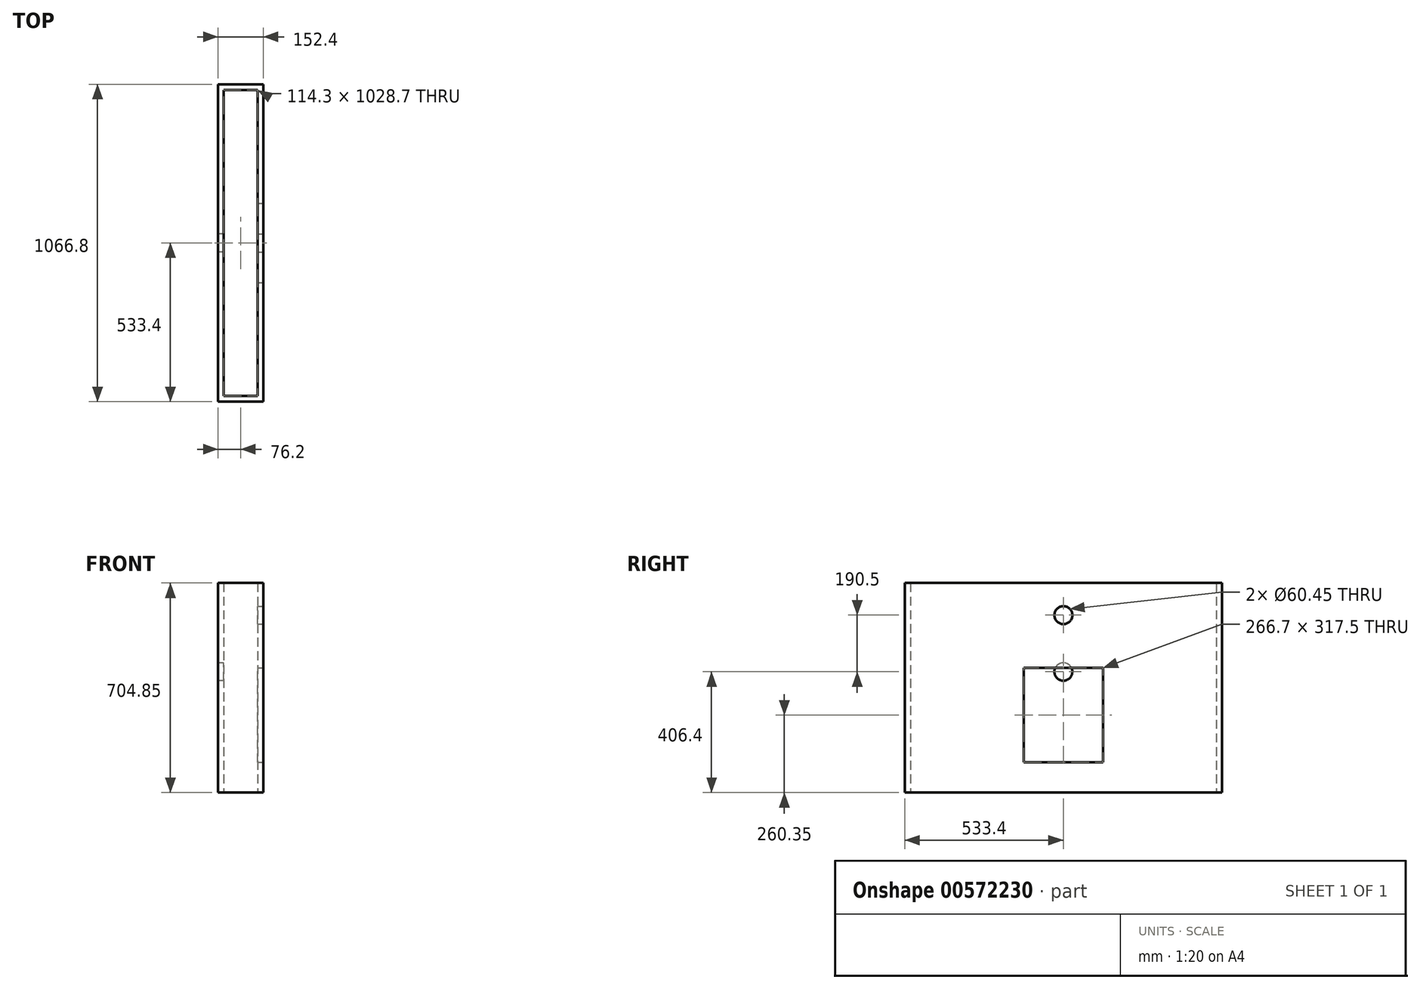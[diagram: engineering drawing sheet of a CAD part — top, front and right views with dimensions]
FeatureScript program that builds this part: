
annotation { "Feature Type Name" : "Feature", "Feature Type Description" : "" }
export const myFeature = defineFeature(function(context is Context, id is Id, definition is map)
    precondition{}
    {
        {
            var Q0;
            Q0=qCreatedBy(makeId("Top.planeOp"),FACE);
            var sketch = newSketch(context, id + "F0", { "sketchPlane" : qUnion([Q0])});
            skLineSegment(sketch, "E0.bottom", {"start": v(76.2, 533.4) * mm, "end": v(-76.2, 533.4) * mm});
            skLineSegment(sketch, "E0.top", {"start": v(76.2, -533.4) * mm, "end": v(-76.2, -533.4) * mm});
            skLineSegment(sketch, "E0.left", {"start": v(76.2, 533.4) * mm, "end": v(76.2, -533.4) * mm});
            skLineSegment(sketch, "E0.right", {"start": v(-76.2, 533.4) * mm, "end": v(-76.2, -533.4) * mm});
            skPoint(sketch, "E0.middle", {"position": v(0, 0) * mm});
            skLineSegment(sketch, "E1.bottom", {"start": v(57.15, 514.35) * mm, "end": v(-57.15, 514.35) * mm});
            skLineSegment(sketch, "E1.top", {"start": v(57.15, -514.35) * mm, "end": v(-57.15, -514.35) * mm});
            skLineSegment(sketch, "E1.left", {"start": v(57.15, 514.35) * mm, "end": v(57.15, -514.35) * mm});
            skLineSegment(sketch, "E1.right", {"start": v(-57.15, 514.35) * mm, "end": v(-57.15, -514.35) * mm});
            skSolve(sketch);
        }
        {
            var Q0;
            Q0=makeQuery(id+"F0.imprint","IMPRINT",FACE,{"disambiguationData":[TD([[makeQuery(id+"F0.imprint","IMPRINT",EDGE,{"derivedFrom":sQuery(id+"F0.wireOp",EDGE,"E0.bottom")}),1.0]])]});
            extrude(context, id + "F1", {"entities" : qUnion([Q0]), "depth" : 704.85 * mm, "offsetDistance" : 25.4 * mm});
        }
        {
            var Q0;
            Q0=makeQuery(id+"F1.opExtrude","SWEPT_FACE",FACE,{"disambiguationData":[OSD([sQuery(id+"F0.wireOp",EDGE,"E0.left")])]});
            var sketch = newSketch(context, id + "F2", { "sketchPlane" : qUnion([Q0])});
            skLineSegment(sketch, "E2", {"start": v(0, 0) * mm, "end": v(0, 101.6) * mm});
            skPoint(sketch, "E2.endSnap0", {"position": v(0, 0) * mm});
            skLineSegment(sketch, "E3", {"start": v(0, 101.6) * mm, "end": v(0, 260.35) * mm});
            skLineSegment(sketch, "E4.bottom", {"start": v(133.35, 101.6) * mm, "end": v(-133.35, 101.6) * mm});
            skLineSegment(sketch, "E4.top", {"start": v(133.35, 419.1) * mm, "end": v(-133.35, 419.1) * mm});
            skLineSegment(sketch, "E4.left", {"start": v(133.35, 101.6) * mm, "end": v(133.35, 419.1) * mm});
            skLineSegment(sketch, "E4.right", {"start": v(-133.35, 101.6) * mm, "end": v(-133.35, 419.1) * mm});
            skPoint(sketch, "E4.middle", {"position": v(0, 260.35) * mm});
            skLineSegment(sketch, "E5", {"start": v(0, 419.1) * mm, "end": v(0, 596.9) * mm});
            skPoint(sketch, "E5.endSnap0", {"position": v(0, 419.1) * mm});
            skCircle(sketch, "E6", {"center": v(0, 596.9) * mm, "radius": 30.23 * mm});
            skPoint(sketch, "E7.endSnap0", {"position": v(0, 704.85) * mm});
            skSolve(sketch);
        }
        {
            var Q0;
            Q0=makeQuery(id+"F2.imprint","IMPRINT",FACE,{"disambiguationData":[TD([[makeQuery(id+"F2.imprint","IMPRINT",EDGE,{"derivedFrom":sQuery(id+"F2.wireOp",EDGE,"GGn8ku5c-GKVz-RgPz-p5no-ucrrB1cT99kD")}),1.0]])]});
            var Q1;
            Q1=makeQuery(id+"F2.imprint","IMPRINT",FACE,{"disambiguationData":[TD([[makeQuery(id+"F2.imprint","IMPRINT",EDGE,{"derivedFrom":sQuery(id+"F2.wireOp",EDGE,"E6")}),1.0]])]});
            var Q2;
            {var subQ3=sQuery(id+"F2.wireOp",EDGE,"E4.left");Q2=makeQuery(id+"F2.imprint","IMPRINT",FACE,{"disambiguationData":[TD([[makeQuery(id+"F2.imprint","IMPRINT",EDGE,{"derivedFrom":subQ3}),1.0]])]});}
            extrude(context, id + "F3", {"entities" : qUnion([Q0, Q1, Q2]), "operationType" : NewBodyOperationType.REMOVE, "oppositeDirection" : true, "depth" : 25.4 * mm, "offsetDistance" : 25.4 * mm});
        }
        {
            var Q0;
            Q0=makeQuery(id+"F1.opExtrude","SWEPT_FACE",FACE,{"disambiguationData":[OSD([sQuery(id+"F0.wireOp",EDGE,"E0.right")])]});
            var sketch = newSketch(context, id + "F4", { "sketchPlane" : qUnion([Q0])});
            skLineSegment(sketch, "E8", {"start": v(0, 0) * mm, "end": v(0, 406.4) * mm});
            skCircle(sketch, "E9", {"center": v(0, 406.4) * mm, "radius": 30.23 * mm});
            skSolve(sketch);
        }
        {
            var Q0;
            Q0=makeQuery(id+"F4.imprint","IMPRINT",FACE,{"disambiguationData":[TD([[makeQuery(id+"F4.imprint","IMPRINT",EDGE,{"derivedFrom":sQuery(id+"F4.wireOp",EDGE,"E9")}),1.0]])]});
            extrude(context, id + "F5", {"entities" : qUnion([Q0]), "operationType" : NewBodyOperationType.REMOVE, "oppositeDirection" : true, "depth" : 25.4 * mm, "offsetDistance" : 25.4 * mm});
        }
    });
